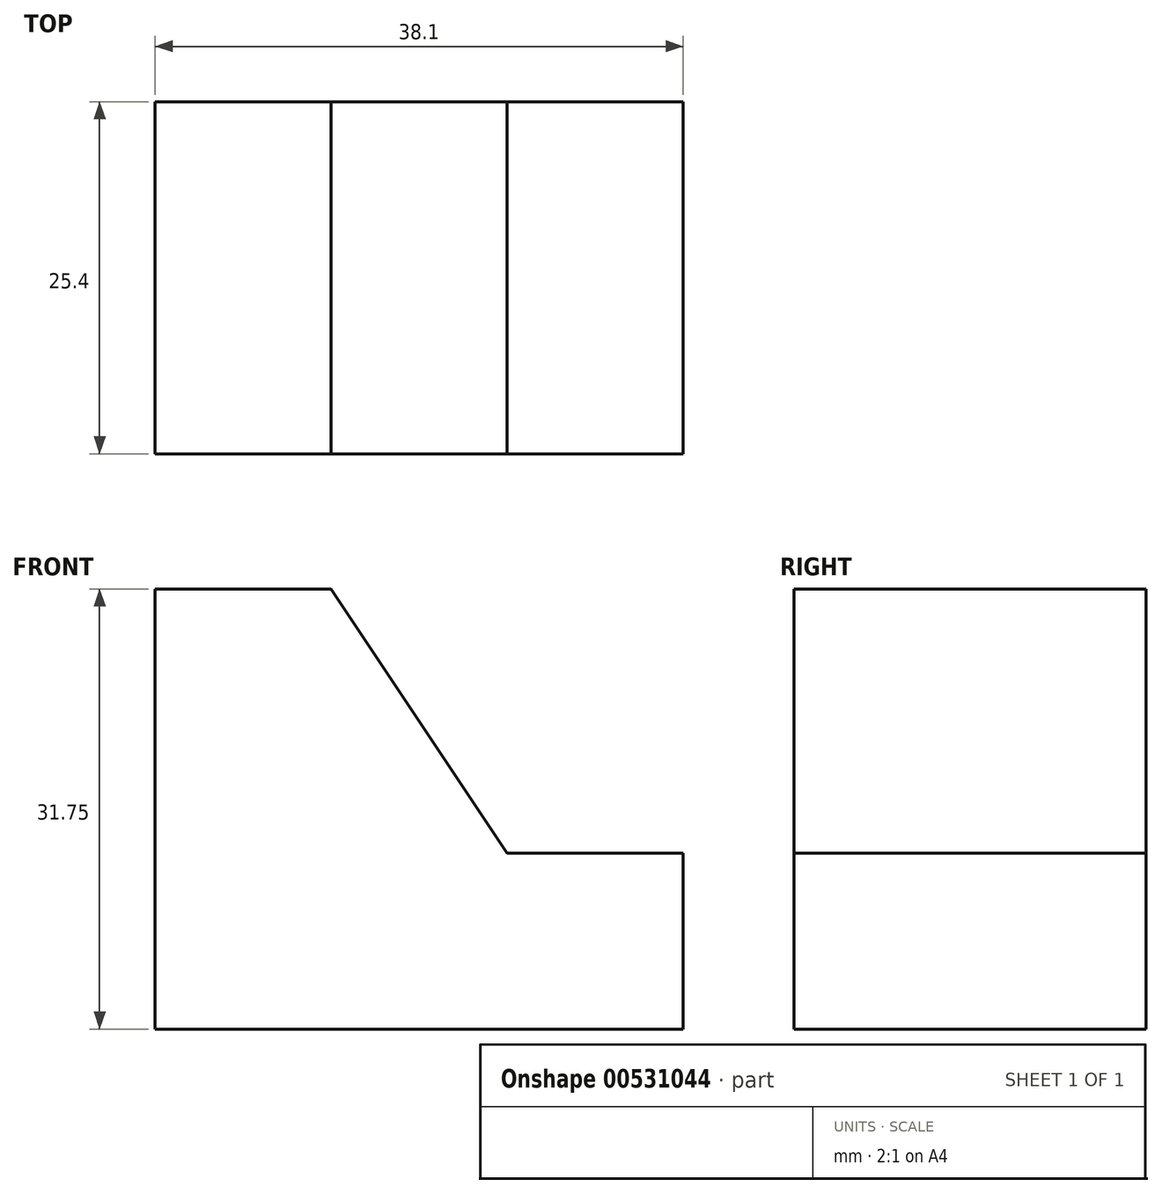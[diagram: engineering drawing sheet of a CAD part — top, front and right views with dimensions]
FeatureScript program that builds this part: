
annotation { "Feature Type Name" : "Feature", "Feature Type Description" : "" }
export const myFeature = defineFeature(function(context is Context, id is Id, definition is map)
    precondition{}
    {
        {
            var Q0;
            Q0=qCreatedBy(makeId("Right.planeOp"),FACE);
            var sketch = newSketch(context, id + "F0", { "sketchPlane" : qUnion([Q0])});
            skLineSegment(sketch, "E0", {"start": v(0, 0) * mm, "end": v(25.4, 0) * mm});
            skLineSegment(sketch, "E1", {"start": v(25.4, 0) * mm, "end": v(25.4, 31.75) * mm});
            skLineSegment(sketch, "E2", {"start": v(25.4, 31.75) * mm, "end": v(0, 31.75) * mm});
            skLineSegment(sketch, "E3", {"start": v(0, 31.75) * mm, "end": v(0, 0) * mm});
            skSolve(sketch);
        }
        {
            var Q0;
            Q0=makeQuery(id+"F0.imprint","IMPRINT",FACE,{"disambiguationData":[TD([[makeQuery(id+"F0.imprint","IMPRINT",EDGE,{"derivedFrom":sQuery(id+"F0.wireOp",EDGE,"E0")}),1.0]])]});
            extrude(context, id + "F1", {"entities" : qUnion([Q0]), "depth" : 38.1 * mm, "offsetDistance" : 25.4 * mm});
        }
        {
            var Q0;
            Q0=makeQuery(id+"F1.opExtrude","SWEPT_FACE",FACE,{"disambiguationData":[OSD([sQuery(id+"F0.wireOp",EDGE,"E3")])]});
            var sketch = newSketch(context, id + "F2", { "sketchPlane" : qUnion([Q0])});
            skLineSegment(sketch, "E4", {"start": v(12.7, 31.75) * mm, "end": v(25.4, 12.7) * mm});
            skLineSegment(sketch, "E5", {"start": v(25.4, 12.7) * mm, "end": v(38.1, 12.7) * mm});
            skSolve(sketch);
        }
        {
            var Q0;
            {var subQ0=sQuery(id+"F2.wireOp",EDGE,"E4");Q0=makeQuery(id+"F2.imprint","IMPRINT",FACE,{"disambiguationData":[TD([[makeQuery(id+"F2.imprint","IMPRINT",EDGE,{"derivedFrom":subQ0}),1.0]])]});}
            extrude(context, id + "F3", {"entities" : qUnion([Q0]), "operationType" : NewBodyOperationType.REMOVE, "oppositeDirection" : true, "depth" : 25.4 * mm, "offsetDistance" : 25.4 * mm});
        }
    });
